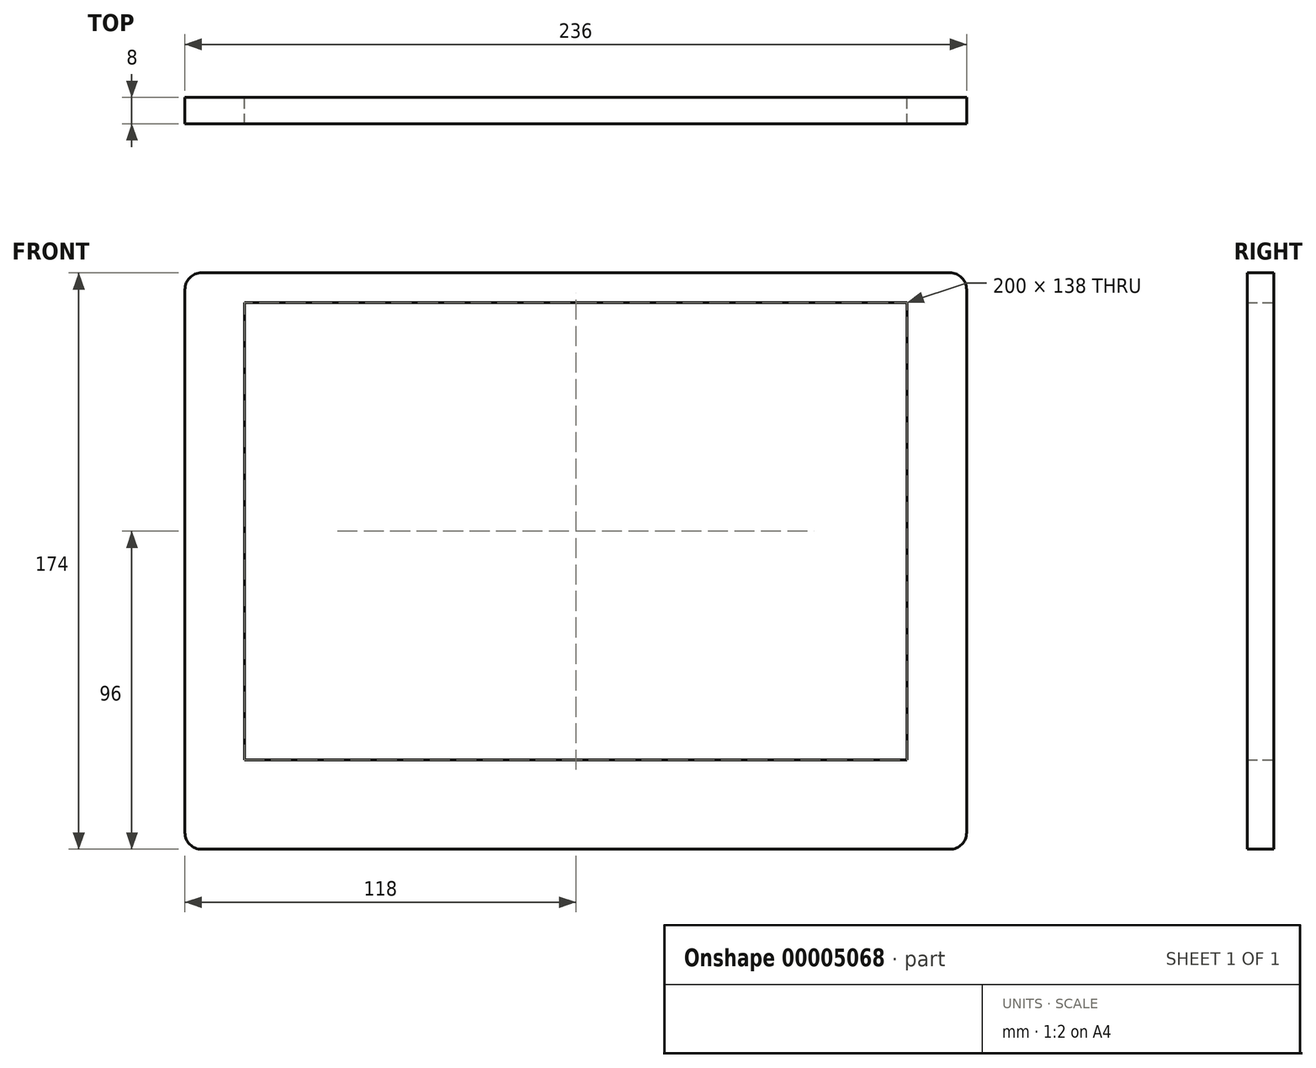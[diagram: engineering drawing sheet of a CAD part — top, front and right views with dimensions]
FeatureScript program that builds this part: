
annotation { "Feature Type Name" : "Feature", "Feature Type Description" : "" }
export const myFeature = defineFeature(function(context is Context, id is Id, definition is map)
    precondition{}
    {
        {
            var Q0;
            Q0=qCreatedBy(makeId("Front.planeOp"),FACE);
            var sketch = newSketch(context, id + "F0", { "sketchPlane" : qUnion([Q0])});
            skLineSegment(sketch, "E0.rect.bottom", {"start": v(118, -87) * mm, "end": v(-118, -87) * mm});
            skLineSegment(sketch, "E0.rect.top", {"start": v(118, 87) * mm, "end": v(-118, 87) * mm});
            skLineSegment(sketch, "E0.rect.left", {"start": v(118, -87) * mm, "end": v(118, 87) * mm});
            skLineSegment(sketch, "E0.rect.right", {"start": v(-118, -87) * mm, "end": v(-118, 87) * mm});
            skPoint(sketch, "E0.rect.middle", {"position": v(0, 0) * mm});
            skLineSegment(sketch, "E1.rect.bottom", {"start": v(100, -60) * mm, "end": v(-100, -60) * mm});
            skLineSegment(sketch, "E1.rect.top", {"start": v(100, 78) * mm, "end": v(-100, 78) * mm});
            skLineSegment(sketch, "E1.rect.left", {"start": v(100, -60) * mm, "end": v(100, 78) * mm});
            skLineSegment(sketch, "E1.rect.right", {"start": v(-100, -60) * mm, "end": v(-100, 78) * mm});
            skPoint(sketch, "E1.rect.middle", {"position": v(0, 9) * mm});
            skSolve(sketch);
        }
        {
            var Q0;
            Q0=qSketchRegion(id+"F0",true);
            extrude(context, id + "F1", {"entities" : qUnion([Q0]), "depth" : 8 * mm});
        }
        {
            var Q0;
            Q0=makeQuery(id+"F1.opExtrude","SWEPT_EDGE",EDGE,{"disambiguationData":[OSD([sQuery(id+"F0.wireOp",EDGE,"E0.rect.top"),sQuery(id+"F0.wireOp",EDGE,"E0.rect.right")])]});
            var Q1;
            Q1=makeQuery(id+"F1.opExtrude","SWEPT_EDGE",EDGE,{"disambiguationData":[OSD([sQuery(id+"F0.wireOp",EDGE,"E0.rect.top"),sQuery(id+"F0.wireOp",EDGE,"E0.rect.left")])]});
            var Q2;
            Q2=makeQuery(id+"F1.opExtrude","SWEPT_EDGE",EDGE,{"disambiguationData":[OSD([sQuery(id+"F0.wireOp",EDGE,"E0.rect.bottom"),sQuery(id+"F0.wireOp",EDGE,"E0.rect.left")])]});
            var Q3;
            Q3=makeQuery(id+"F1.opExtrude","SWEPT_EDGE",EDGE,{"disambiguationData":[OSD([sQuery(id+"F0.wireOp",EDGE,"E0.rect.bottom"),sQuery(id+"F0.wireOp",EDGE,"E0.rect.right")])]});
            fillet(context, id + "F2", {"entities" : qUnion([Q0, Q1, Q2, Q3]), "radius" : 5 * mm, "tangentPropagation" : true, "allowEdgeOverflow" : false});
        }
    });
